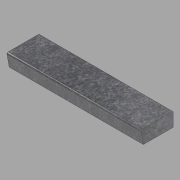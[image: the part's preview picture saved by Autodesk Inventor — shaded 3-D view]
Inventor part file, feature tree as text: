
AUTODESK INVENTOR PART (.ipt)
format: ipt  version: 2022.1 (Build 261234020, 234B)  size: 99,328 bytes
history: native  units: in
note: dims shown in document units (in); Inventor stores cm internally (conversion verified against a paired STEP export)
features: other x3, extrude x1, sketch x1
ambient origin geometry x8: Origin, YZ Plane, XZ Plane, XY Plane, X Axis, Y Axis, Z Axis, Center Point
bodies: Solid1 (feature_tree)
feature tree (5):
  other  "Blocks"
  extrude  "Extrusion1"  Depth=58.75in TaperAngle=0.0deg
  sketch  "Sketch1"  dims[d0=13.0in d1=6.0in d2=13.5in d3=0.5in d4=0.5in d5=58.75in d6=0.0in]
  other  "Profile"
  other  "Profile:1"
